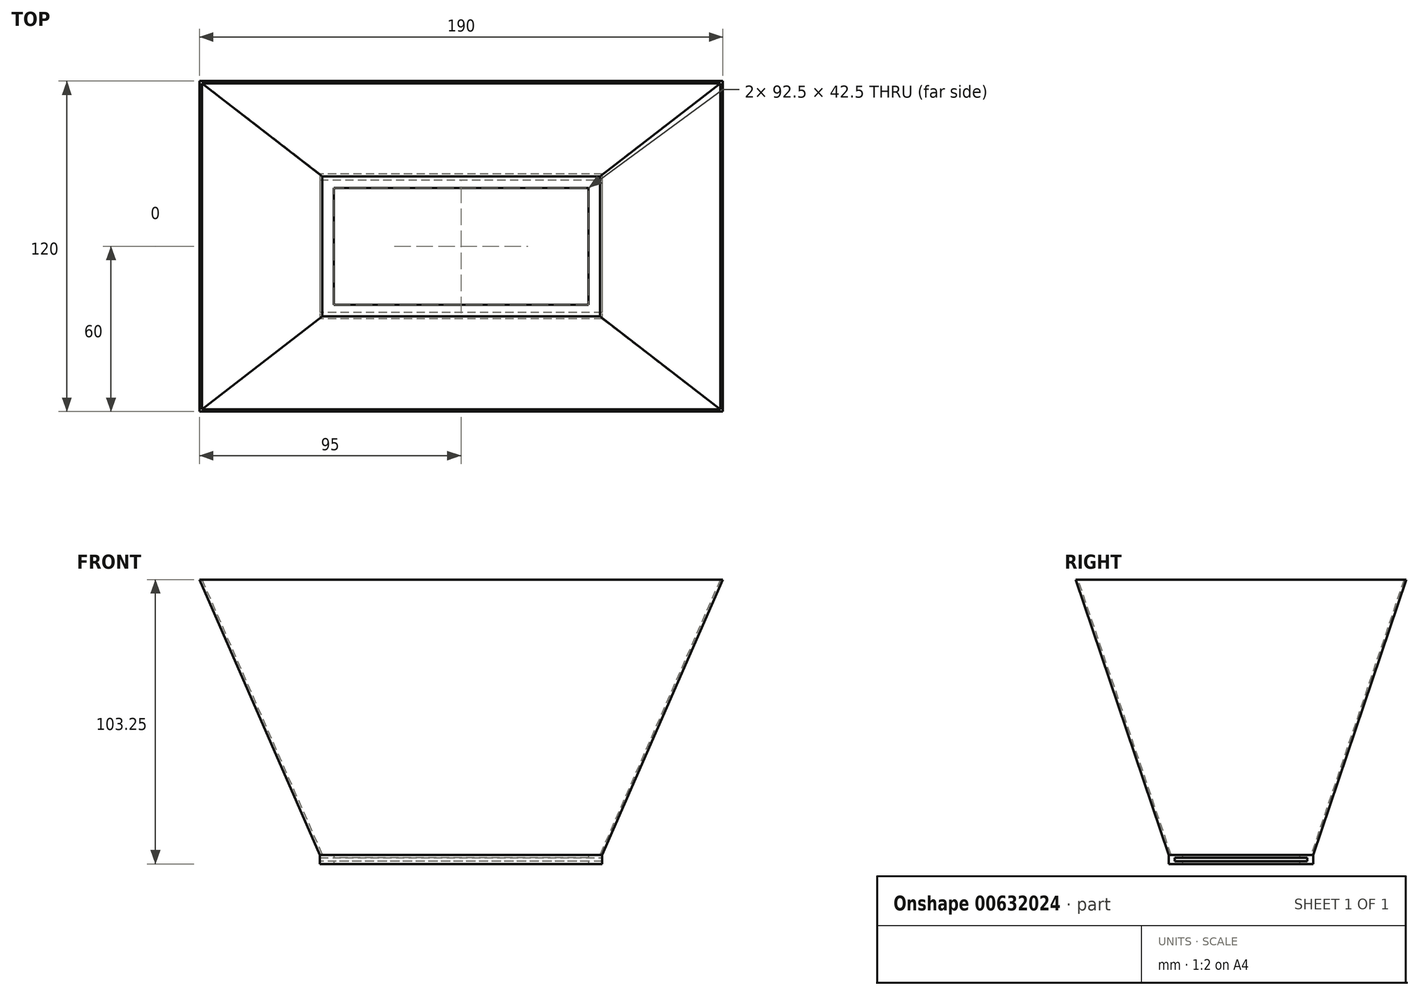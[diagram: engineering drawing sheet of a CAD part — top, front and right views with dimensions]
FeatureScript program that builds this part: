
annotation { "Feature Type Name" : "Feature", "Feature Type Description" : "" }
export const myFeature = defineFeature(function(context is Context, id is Id, definition is map)
    precondition{}
    {
        {
            var Q0;
            Q0=qCreatedBy(makeId("Top.planeOp"),FACE);
            var sketch = newSketch(context, id + "F0", { "sketchPlane" : qUnion([Q0])});
            skLineSegment(sketch, "E0.bottom", {"start": v(51.25, 26.25) * mm, "end": v(-51.25, 26.25) * mm});
            skLineSegment(sketch, "E0.top", {"start": v(51.25, -26.25) * mm, "end": v(-51.25, -26.25) * mm});
            skLineSegment(sketch, "E0.left", {"start": v(51.25, 26.25) * mm, "end": v(51.25, -26.25) * mm});
            skLineSegment(sketch, "E0.right", {"start": v(-51.25, 26.25) * mm, "end": v(-51.25, -26.25) * mm});
            skPoint(sketch, "E0.middle", {"position": v(0, 0) * mm});
            skLineSegment(sketch, "E1.bottom", {"start": v(46.25, 21.25) * mm, "end": v(-46.25, 21.25) * mm});
            skLineSegment(sketch, "E1.top", {"start": v(46.25, -21.25) * mm, "end": v(-46.25, -21.25) * mm});
            skLineSegment(sketch, "E1.left", {"start": v(46.25, 21.25) * mm, "end": v(46.25, -21.25) * mm});
            skLineSegment(sketch, "E1.right", {"start": v(-46.25, 21.25) * mm, "end": v(-46.25, -21.25) * mm});
            skSolve(sketch);
        }
        {
            var Q0;
            Q0 = qSketchRegion(id + "F0", true);
            extrude(context, id + "F1", {"entities" : qUnion([Q0]), "depth" : 1 * mm, "offsetDistance" : 25 * mm});
        }
        {
            var Q0;
            Q0=makeQuery(id+"F1.opExtrude","CAP_FACE",FACE,{"disambiguationData":[OSD([sQuery(id+"F0.wireOp",EDGE,"E0.bottom"),sQuery(id+"F0.wireOp",EDGE,"E0.top"),sQuery(id+"F0.wireOp",EDGE,"E0.left"),sQuery(id+"F0.wireOp",EDGE,"E0.right"),sQuery(id+"F0.wireOp",EDGE,"E1.bottom"),sQuery(id+"F0.wireOp",EDGE,"E1.top"),sQuery(id+"F0.wireOp",EDGE,"E1.left"),sQuery(id+"F0.wireOp",EDGE,"E1.right")])],"isStart":false});
            var sketch = newSketch(context, id + "F2", { "sketchPlane" : qUnion([Q0])});
            skLineSegment(sketch, "E2.bottom", {"start": v(-51.25, 26.25) * mm, "end": v(51.25, 26.25) * mm});
            skLineSegment(sketch, "E2.top", {"start": v(-51.25, 24.05) * mm, "end": v(51.25, 24.05) * mm});
            skLineSegment(sketch, "E2.left", {"start": v(-51.25, 26.25) * mm, "end": v(-51.25, 24.05) * mm});
            skLineSegment(sketch, "E2.right", {"start": v(51.25, 26.25) * mm, "end": v(51.25, 24.05) * mm});
            skLineSegment(sketch, "E3.bottom", {"start": v(51.25, -26.25) * mm, "end": v(-51.25, -26.25) * mm});
            skLineSegment(sketch, "E3.top", {"start": v(51.25, -24.05) * mm, "end": v(-51.25, -24.05) * mm});
            skLineSegment(sketch, "E3.left", {"start": v(51.25, -26.25) * mm, "end": v(51.25, -24.05) * mm});
            skLineSegment(sketch, "E3.right", {"start": v(-51.25, -26.25) * mm, "end": v(-51.25, -24.05) * mm});
            skSolve(sketch);
        }
        {
            var Q0;
            Q0 = qSketchRegion(id + "F2", true);
            extrude(context, id + "F3", {"entities" : qUnion([Q0]), "operationType" : NewBodyOperationType.ADD, "depth" : 1.25 * mm, "offsetDistance" : 25 * mm});
        }
        {
            var Q0;
            Q0=makeQuery(id+"F3.opExtrude","CAP_FACE",FACE,{"disambiguationData":[OSD([sQuery(id+"F2.wireOp",EDGE,"E2.bottom"),sQuery(id+"F2.wireOp",EDGE,"E2.top"),sQuery(id+"F2.wireOp",EDGE,"E2.left"),sQuery(id+"F2.wireOp",EDGE,"E2.right")])],"isStart":false});
            var sketch = newSketch(context, id + "F4", { "sketchPlane" : qUnion([Q0])});
            skPoint(sketch, "E4.0", {"position": v(51.25, -26.25) * mm});
            skLineSegment(sketch, "E5.bottom", {"start": v(51.25, -26.25) * mm, "end": v(-51.25, -26.25) * mm});
            skLineSegment(sketch, "E5.top", {"start": v(51.25, 26.25) * mm, "end": v(-51.25, 26.25) * mm});
            skLineSegment(sketch, "E5.left", {"start": v(51.25, -26.25) * mm, "end": v(51.25, 26.25) * mm});
            skLineSegment(sketch, "E5.right", {"start": v(-51.25, -26.25) * mm, "end": v(-51.25, 26.25) * mm});
            skLineSegment(sketch, "E6.0", {"start": v(-46.25, -21.25) * mm, "end": v(-46.25, 21.25) * mm});
            skLineSegment(sketch, "E6.1", {"start": v(46.25, -21.25) * mm, "end": v(-46.25, -21.25) * mm});
            skLineSegment(sketch, "E6.2", {"start": v(46.25, -21.25) * mm, "end": v(46.25, 21.25) * mm});
            skLineSegment(sketch, "E6.3", {"start": v(46.25, 21.25) * mm, "end": v(-46.25, 21.25) * mm});
            skSolve(sketch);
        }
        {
            var Q0;
            Q0 = qSketchRegion(id + "F4", true);
            var Q1;
            {var subQ0=sQuery(id+"F4.wireOp",EDGE,"NDb1J6HV-2Xbp-x7l8-0kLC-0GCicat0fAFB");Q1=makeQuery(id+"F4.imprint","IMPRINT",FACE,{"disambiguationData":[TD([[makeQuery(id+"F4.imprint","IMPRINT",EDGE,{"derivedFrom":subQ0}),1.0]])]});}
            extrude(context, id + "F5", {"entities" : qUnion([Q0, Q1]), "operationType" : NewBodyOperationType.ADD, "depth" : 1 * mm, "offsetDistance" : 25 * mm});
        }
        {
            var Q0;
            Q0=makeQuery(id+"F5.opExtrude","CAP_FACE",FACE,{"disambiguationData":[OSD([sQuery(id+"F4.wireOp",EDGE,"E5.bottom"),sQuery(id+"F4.wireOp",EDGE,"E5.top"),sQuery(id+"F4.wireOp",EDGE,"E5.left"),sQuery(id+"F4.wireOp",EDGE,"E5.right"),sQuery(id+"F4.wireOp",EDGE,"E6.0"),sQuery(id+"F4.wireOp",EDGE,"E6.1"),sQuery(id+"F4.wireOp",EDGE,"E6.2"),sQuery(id+"F4.wireOp",EDGE,"E6.3"),sQuery(id+"F4.wireOp",EDGE,"NDb1J6HV-2Xbp-x7l8-0kLC-0GCicat0fAFB"),sQuery(id+"F4.wireOp",EDGE,"gbTYzVVf-XM4L-eotd-PRIW-pzFDhGdd6Xwr")])],"isStart":false});
            var sketch = newSketch(context, id + "F6", { "sketchPlane" : qUnion([Q0])});
            skLineSegment(sketch, "E7.0", {"start": v(51.25, 26.25) * mm, "end": v(-51.25, 26.25) * mm});
            skLineSegment(sketch, "E7.1", {"start": v(-51.25, 26.25) * mm, "end": v(-51.25, -26.25) * mm});
            skLineSegment(sketch, "E7.2", {"start": v(51.25, 26.25) * mm, "end": v(51.25, -26.25) * mm});
            skLineSegment(sketch, "E7.3", {"start": v(51.25, -26.25) * mm, "end": v(-51.25, -26.25) * mm});
            skSolve(sketch);
        }
        {
            var Q0;
            Q0=makeQuery(id+"F5.opExtrude","CAP_FACE",FACE,{"disambiguationData":[OSD([sQuery(id+"F4.wireOp",EDGE,"E5.bottom"),sQuery(id+"F4.wireOp",EDGE,"E5.top"),sQuery(id+"F4.wireOp",EDGE,"E5.left"),sQuery(id+"F4.wireOp",EDGE,"E5.right"),sQuery(id+"F4.wireOp",EDGE,"E6.0"),sQuery(id+"F4.wireOp",EDGE,"E6.1"),sQuery(id+"F4.wireOp",EDGE,"E6.2"),sQuery(id+"F4.wireOp",EDGE,"E6.3"),sQuery(id+"F4.wireOp",EDGE,"NDb1J6HV-2Xbp-x7l8-0kLC-0GCicat0fAFB"),sQuery(id+"F4.wireOp",EDGE,"gbTYzVVf-XM4L-eotd-PRIW-pzFDhGdd6Xwr")])],"isStart":false});
            cPlane(context, id + "F7", {"entities" : qUnion([Q0]), "cplaneType" : CPlaneType.OFFSET, "offset" : 100 * mm, "width" : 150 * mm, "height" : 150 * mm});
        }
        {
            var Q0;
            Q0=qCreatedBy(id+"F7.planeOp",FACE);
            var sketch = newSketch(context, id + "F8", { "sketchPlane" : qUnion([Q0])});
            skLineSegment(sketch, "E8.bottom", {"start": v(95, 60) * mm, "end": v(-95, 60) * mm});
            skLineSegment(sketch, "E8.top", {"start": v(95, -60) * mm, "end": v(-95, -60) * mm});
            skLineSegment(sketch, "E8.left", {"start": v(95, 60) * mm, "end": v(95, -60) * mm});
            skLineSegment(sketch, "E8.right", {"start": v(-95, 60) * mm, "end": v(-95, -60) * mm});
            skPoint(sketch, "E8.middle", {"position": v(0, 0) * mm});
            skSolve(sketch);
        }
        {
            var Q1;
            Q1 = qSketchRegion(id + "F6", true);
            var Q2;
            Q2 = qSketchRegion(id + "F8", true);
            loft(context, id + "F9", {"sheetProfilesArray" : [{ "sheetProfileEntities" : qUnion([Q1]) }, { "sheetProfileEntities" : qUnion([Q2]) }]});
        }
        {
            var Q0;
            Q0=makeQuery(id+"F9.opLoft","CAP_FACE",FACE,{"disambiguationData":[OSD([makeQuery(id+"F8.imprint","IMPRINT",FACE,{"disambiguationData":[TD([[makeQuery(id+"F8.imprint","IMPRINT",EDGE,{"derivedFrom":sQuery(id+"F8.wireOp",EDGE,"E8.bottom")}),1.0]])]})])],"isStart":true});
            var Q1;
            Q1=makeQuery(id+"F9.opLoft","CAP_FACE",FACE,{"disambiguationData":[OSD([makeQuery(id+"F6.imprint","IMPRINT",FACE,{"disambiguationData":[TD([[makeQuery(id+"F6.imprint","IMPRINT",EDGE,{"derivedFrom":sQuery(id+"F6.wireOp",EDGE,"E7.0")}),1.0]])]})])],"isStart":true});
            var Q2;
            Q2=makeQuery(id+"F9.opLoft","CAP_FACE",FACE,{"disambiguationData":[OSD([makeQuery(id+"F6.imprint","IMPRINT",FACE,{"disambiguationData":[TD([[makeQuery(id+"F6.imprint","IMPRINT",EDGE,{"derivedFrom":makeQuery(id+"F5.opExtrude","CAP_EDGE",EDGE,{"disambiguationData":[OSD([sQuery(id+"F4.wireOp",EDGE,"E6.0")])],"isStart":false})}),-1.0]])]})])],"isStart":true});
            shell(context, id + "F10", {"entities" : qUnion([Q0, Q1, Q2]), "thickness" : 0.8 * mm});
        }
    });
